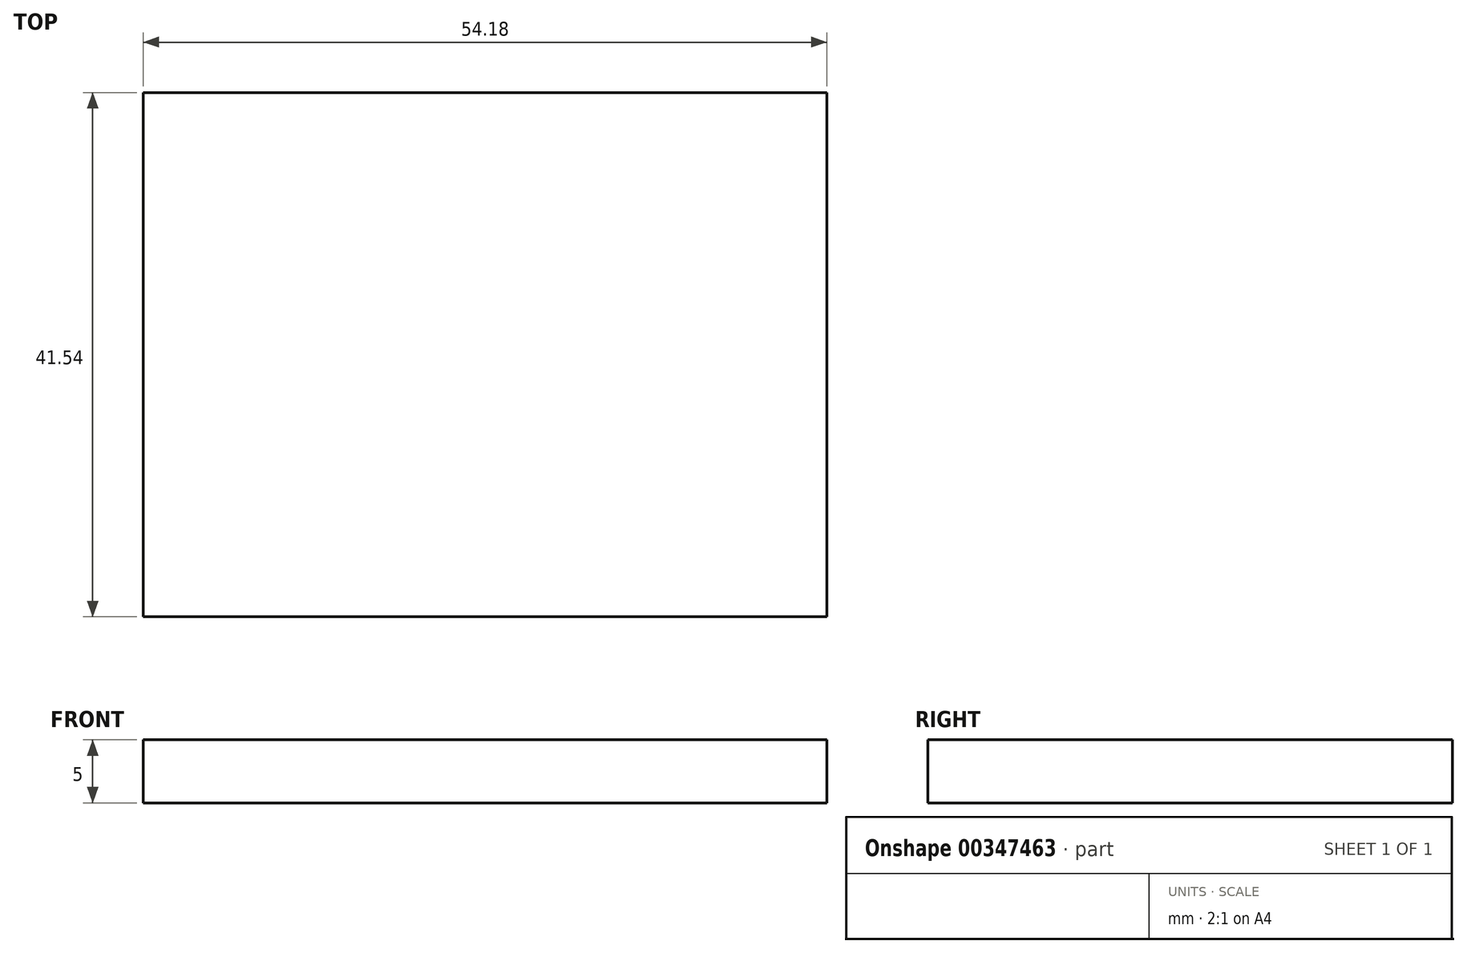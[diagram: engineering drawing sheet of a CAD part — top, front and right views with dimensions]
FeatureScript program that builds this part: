
annotation { "Feature Type Name" : "Feature", "Feature Type Description" : "" }
export const myFeature = defineFeature(function(context is Context, id is Id, definition is map)
    precondition{}
    {
        {
            var Q0;
            Q0=qCreatedBy(makeId("Top.planeOp"),FACE);
            var sketch = newSketch(context, id + "F0", { "sketchPlane" : qUnion([Q0])});
            skLineSegment(sketch, "E0.bottom", {"start": v(27.09, 20.28) * mm, "end": v(-27.09, 20.28) * mm});
            skLineSegment(sketch, "E0.top", {"start": v(27.09, -21.26) * mm, "end": v(-27.09, -21.26) * mm});
            skLineSegment(sketch, "E0.left", {"start": v(27.09, 20.28) * mm, "end": v(27.09, -21.26) * mm});
            skLineSegment(sketch, "E0.right", {"start": v(-27.09, 20.28) * mm, "end": v(-27.09, -21.26) * mm});
            skLineSegment(sketch, "E1", {"start": v(0, 0) * mm, "end": v(0, 20.28) * mm, "construction": true});
            skLineSegment(sketch, "E2", {"start": v(0, 0) * mm, "end": v(-27.09, 0) * mm, "construction": true});
            skPoint(sketch, "E2.endSnap0", {"position": v(-27.09, -0.5) * mm});
            skSolve(sketch);
        }
        {
            var Q0;
            Q0=makeQuery(id+"F0.imprint","IMPRINT",FACE,{"disambiguationData":[TD([[makeQuery(id+"F0.imprint","IMPRINT",EDGE,{"derivedFrom":sQuery(id+"F0.wireOp",EDGE,"E0.bottom")}),1.0]])]});
            extrude(context, id + "F1", {"entities" : qUnion([Q0]), "endBound" : BoundingType.SYMMETRIC, "depth" : 5 * mm});
        }
    });
